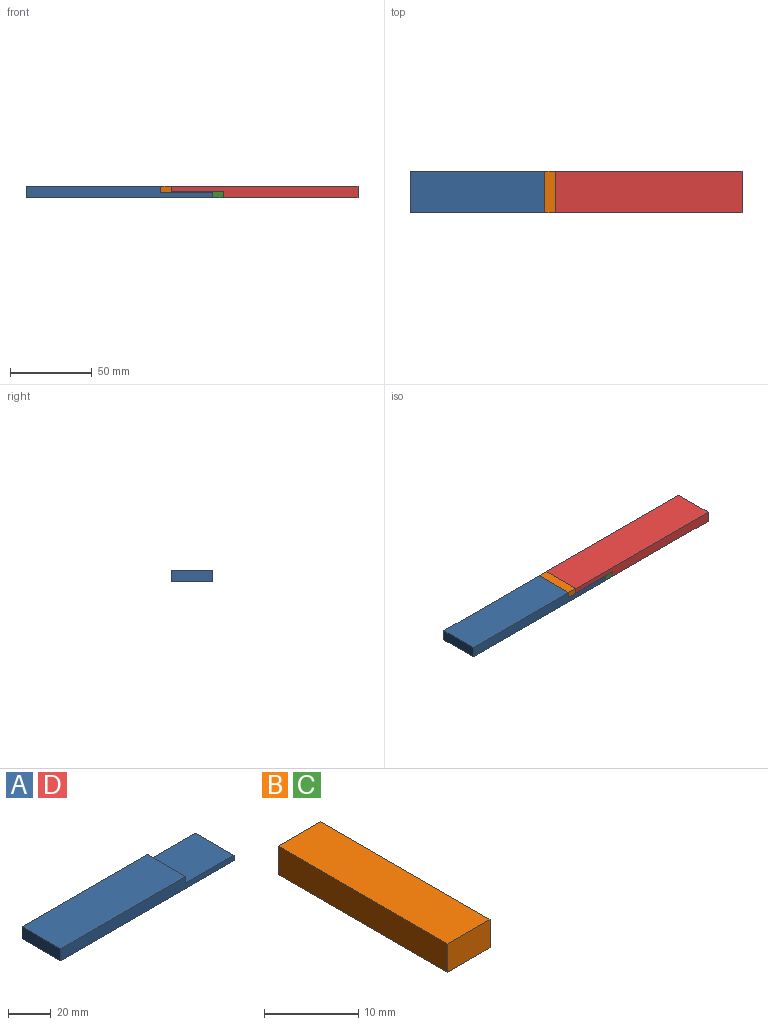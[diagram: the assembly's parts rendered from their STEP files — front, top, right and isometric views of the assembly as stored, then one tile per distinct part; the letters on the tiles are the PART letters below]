
ASSEMBLY  parts=4 mates=9
PART A: 8 faces, bbox 114.3x25.4x6.9 mm
  f0: plane 25.4x6.86mm, normal (-1,0,0), area 174.2mm2, adj f1,f5,f6,f7
  f1: plane 114.3x25.4mm, normal (0,0,-1), area 2903.2mm2, adj f0,f2,f6,f7
  f2: plane 25.4x3.18mm, normal (1,0,0), area 80.6mm2, adj f1,f3,f6,f7
  f3: plane 31.75x25.4mm, normal (0,0,1), area 806.5mm2, adj f2,f4,f6,f7
  f4: plane 25.4x3.68mm, normal (1,0,0), area 93.5mm2, adj f3,f5,f6,f7
  f5: plane 82.55x25.4mm, normal (0,0,1), area 2096.8mm2, adj f0,f4,f6,f7
  f6: plane 114.3x6.86mm, normal (0,-1,0), area 666.9mm2, adj f0,f1,f2,f3,f4,f5
  f7: plane 114.3x6.86mm, normal (0,1,0), area 666.9mm2, adj f0,f1,f2,f3,f4,f5
PART B: 6 faces, bbox 6.4x25.4x3.7 mm
  f0: plane 25.4x6.35mm, normal (0,0,1), area 161.3mm2, adj f1,f3,f4,f5
  f1: plane 25.4x3.68mm, normal (-1,0,0), area 93.5mm2, adj f0,f2,f4,f5
  f2: plane 25.4x6.35mm, normal (0,0,-1), area 161.3mm2, adj f1,f3,f4,f5
  f3: plane 25.4x3.68mm, normal (1,0,0), area 93.5mm2, adj f0,f2,f4,f5
  f4: plane 6.35x3.68mm, normal (0,-1,0), area 23.4mm2, adj f0,f1,f2,f3
  f5: plane 6.35x3.68mm, normal (0,1,0), area 23.4mm2, adj f0,f1,f2,f3
PART C: same geometry as B
PART D: same geometry as A
PLACE A rot(axis=(0,1,0),0deg) t=(-69.12,-7.04,0.73)mm
PLACE B rot(axis=(0,1,0),0deg) t=(-24.67,-7.04,5.75)mm
PLACE C rot(axis=(0,1,0),0deg) t=(7.08,-7.04,2.58)mm
PLACE D rot(axis=(0,-1,0),180deg) t=(51.53,-7.04,7.59)mm
MATE planar B.f3 <-> D.f2  axis (1,0,0) through (-21.49,-19.74,5.75)mm
MATE planar A.f6 <-> D.f6  axis (0,-1,0) through (-53.24,-32.44,0.73)mm
MATE planar A.f5 <-> D.f1  axis (0,0,1) through (-69.12,-19.74,7.59)mm
MATE planar A.f4 <-> B.f1  axis (1,0,0) through (-27.84,-19.74,5.75)mm
MATE planar B.f0 <-> A.f5  axis (0,0,1) through (-21.49,-19.74,7.59)mm
MATE planar C.f4 <-> D.f6  axis (0,-1,0) through (7.08,-32.44,2.58)mm
MATE planar C.f0 <-> D.f3  axis (0,0,1) through (10.26,-19.74,4.42)mm
MATE planar B.f4 <-> A.f6  axis (0,-1,0) through (-24.67,-32.44,5.75)mm
MATE planar C.f1 <-> A.f2  axis (-1,0,0) through (3.91,-19.74,2.58)mm
